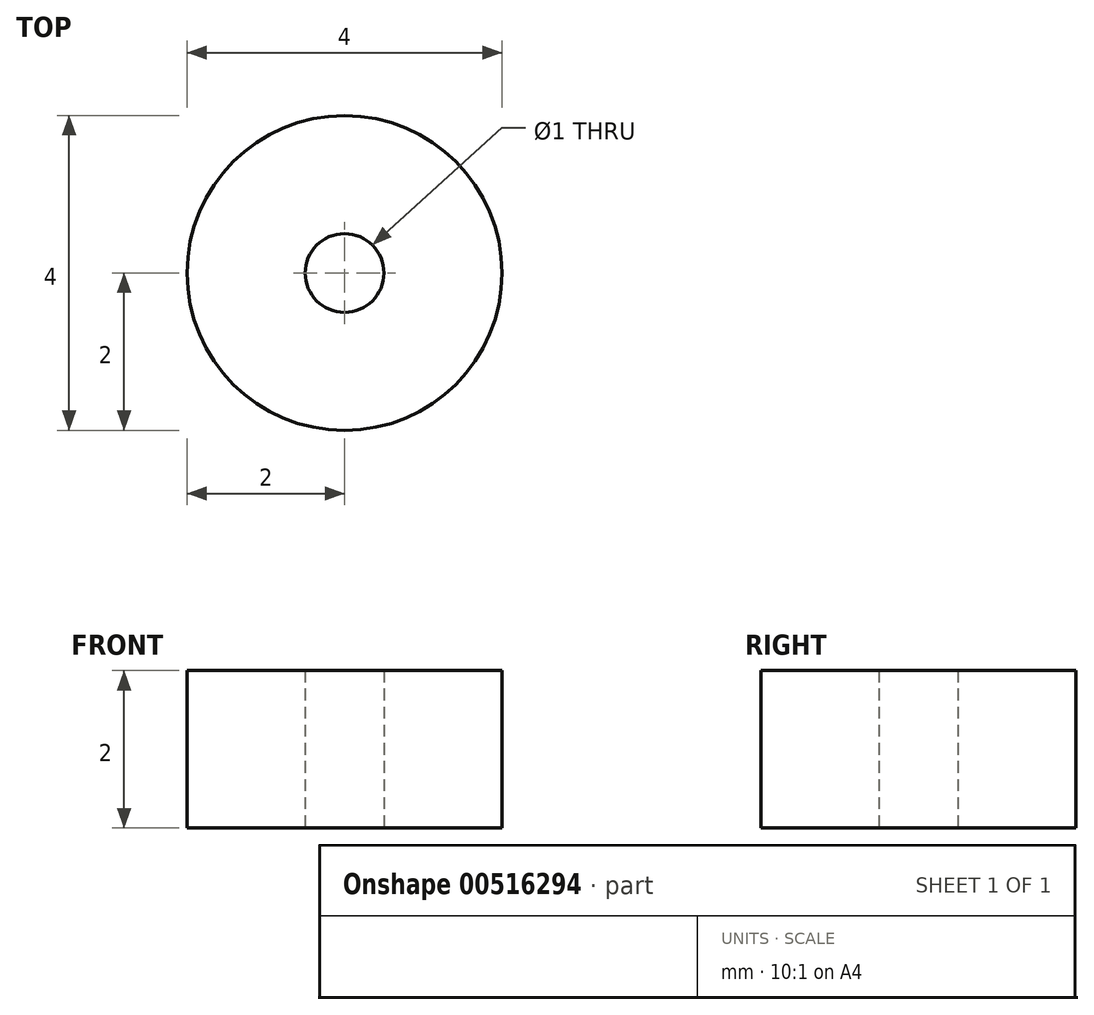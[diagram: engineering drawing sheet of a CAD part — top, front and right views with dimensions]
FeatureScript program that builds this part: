
annotation { "Feature Type Name" : "Feature", "Feature Type Description" : "" }
export const myFeature = defineFeature(function(context is Context, id is Id, definition is map)
    precondition{}
    {
        {
            var Q0;
            Q0=qCreatedBy(makeId("Top.planeOp"),FACE);
            var sketch = newSketch(context, id + "F0", { "sketchPlane" : qUnion([Q0])});
            skCircle(sketch, "E0", {"center": v(0, 0) * mm, "radius": 2 * mm});
            skCircle(sketch, "E1", {"center": v(0, 0) * mm, "radius": 0.5 * mm});
            skSolve(sketch);
        }
        {
            var Q0;
            Q0 = qSketchRegion(id + "F0", true);
            extrude(context, id + "F1", {"entities" : qUnion([Q0]), "depth" : 2 * mm, "offsetDistance" : 25 * mm});
        }
    });
